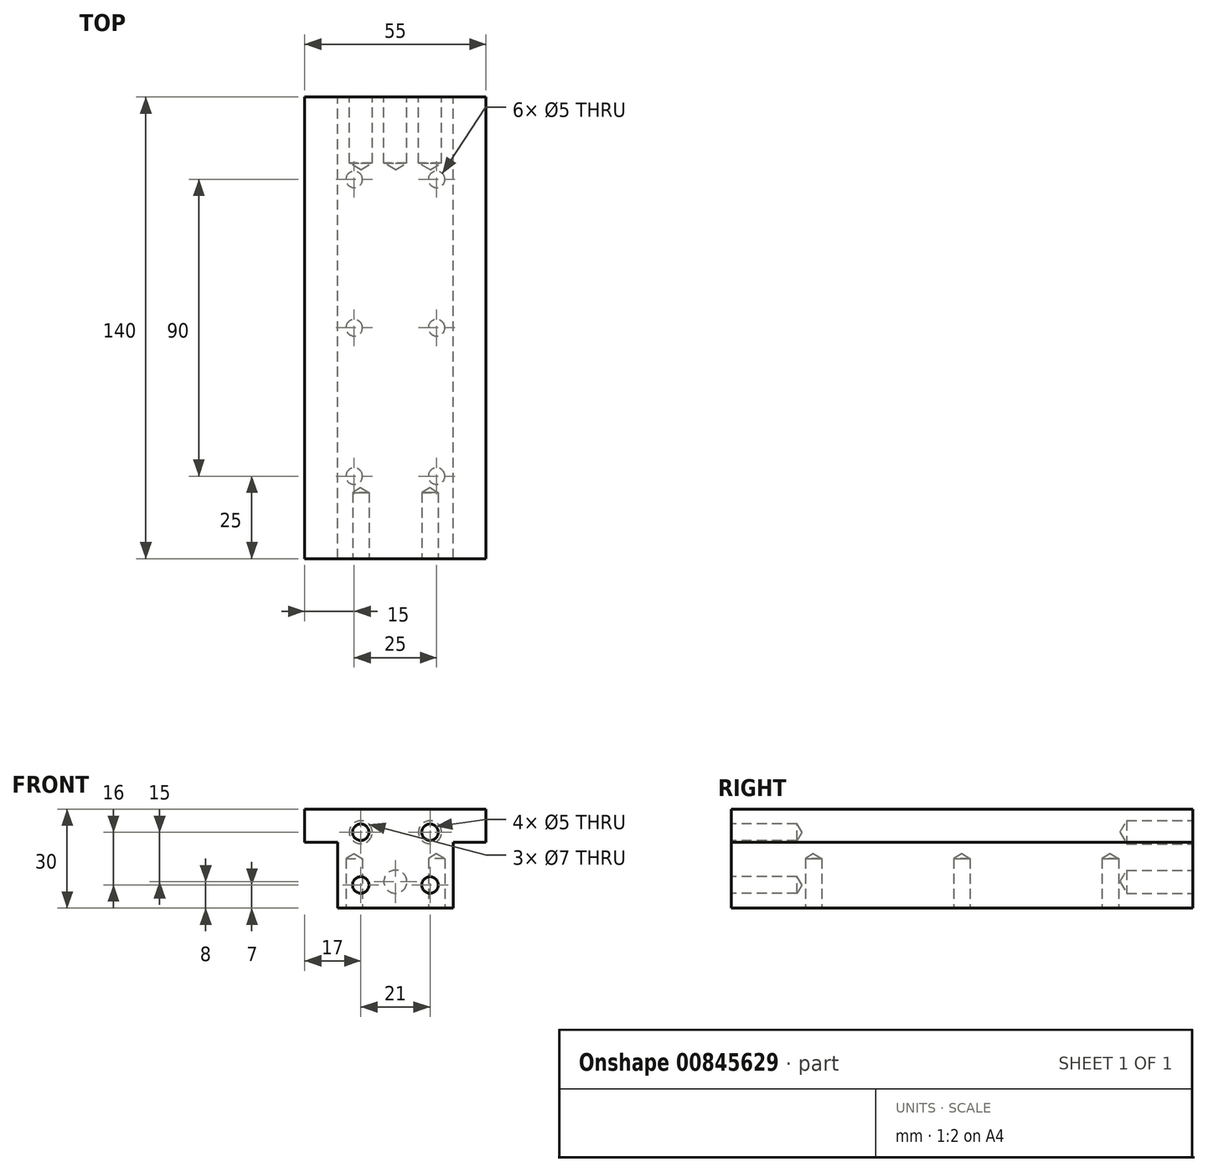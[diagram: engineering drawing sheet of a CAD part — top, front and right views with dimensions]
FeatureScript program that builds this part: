
annotation { "Feature Type Name" : "Feature", "Feature Type Description" : "" }
export const myFeature = defineFeature(function(context is Context, id is Id, definition is map)
    precondition{}
    {
        {
            var Q0;
            Q0=qCreatedBy(makeId("Front.planeOp"),FACE);
            var sketch = newSketch(context, id + "F0", { "sketchPlane" : qUnion([Q0])});
            skLineSegment(sketch, "E0", {"start": v(0, 10) * mm, "end": v(-27.5, 10) * mm});
            skLineSegment(sketch, "E1", {"start": v(-27.5, 10) * mm, "end": v(-27.5, 0) * mm});
            skLineSegment(sketch, "E2", {"start": v(-27.5, 0) * mm, "end": v(-17.5, 0) * mm});
            skLineSegment(sketch, "E3", {"start": v(-17.5, 0) * mm, "end": v(-17.5, -20) * mm});
            skLineSegment(sketch, "E4", {"start": v(-17.5, -20) * mm, "end": v(0, -20) * mm});
            skLineSegment(sketch, "E5", {"start": v(0, -20) * mm, "end": v(0, 10) * mm});
            skSolve(sketch);
        }
        {
            var Q0;
            Q0=makeQuery(id+"F0.imprint","IMPRINT",FACE,{"disambiguationData":[TD([[makeQuery(id+"F0.imprint","IMPRINT",EDGE,{"derivedFrom":sQuery(id+"F0.wireOp",EDGE,"E0")}),1.0]])]});
            extrude(context, id + "F1", {"entities" : qUnion([Q0]), "endBound" : BoundingType.SYMMETRIC, "depth" : 140 * mm, "offsetDistance" : 25 * mm});
        }
        {
            var Q0;
            Q0=makeQuery(id+"F1.opExtrude","CAP_FACE",FACE,{"disambiguationData":[OSD([sQuery(id+"F0.wireOp",EDGE,"E0"),sQuery(id+"F0.wireOp",EDGE,"E1"),sQuery(id+"F0.wireOp",EDGE,"E2"),sQuery(id+"F0.wireOp",EDGE,"E3"),sQuery(id+"F0.wireOp",EDGE,"E4"),sQuery(id+"F0.wireOp",EDGE,"E5")])],"isStart":false});
            var sketch = newSketch(context, id + "F2", { "sketchPlane" : qUnion([Q0])});
            skLineSegment(sketch, "E6", {"start": v(-10.5, 3) * mm, "end": v(-10.5, -13) * mm, "construction": true});
            skSolve(sketch);
        }
        {
            var Q0;
            Q0=sQuery(id+"F2.wireOp",VERTEX,"E6.start");
            var Q1;
            Q1=sQuery(id+"F2.wireOp",VERTEX,"E6.end");
            var Q2;
            Q2=makeQuery(id+"F1.opExtrude","SWEPT_BODY",BODY,{"disambiguationData":[OSD([sQuery(id+"F0.wireOp",EDGE,"E0"),sQuery(id+"F0.wireOp",EDGE,"E1"),sQuery(id+"F0.wireOp",EDGE,"E2"),sQuery(id+"F0.wireOp",EDGE,"E3"),sQuery(id+"F0.wireOp",EDGE,"E4"),sQuery(id+"F0.wireOp",EDGE,"E5")])]});
            hole(context, id + "F3", {"style" : HoleStyle.SIMPLE, "endStyle" : HoleEndStyle.BLIND, "standardTappedOrClearance" : lookupTablePath({ "standard" : "ISO", "engagement" : "75%", "pitch" : "1 mm", "size" : "M6", "type" : "Tapped" }), "standardBlindInLast" : lookupTablePath({ "standard" : "ISO", "engagement" : "75%", "pitch" : "1 mm", "size" : "M6", "type" : "Tapped" }), "holeDiameter" : 5 * mm, "majorDiameter" : 6 * mm, "showTappedDepth" : true, "holeDepth" : 20 * mm, "isTappedThrough" : true, "tappedDepth" : 15 * mm, "tapClearance" : 5, "startFromSketch" : true, "locations" : qUnion([Q0, Q1]), "scope" : qUnion([Q2])});
        }
        {
            var Q0;
            Q0=makeQuery(id+"F1.opExtrude","SWEPT_FACE",FACE,{"disambiguationData":[OSD([sQuery(id+"F0.wireOp",EDGE,"E4")])]});
            var sketch = newSketch(context, id + "F4", { "sketchPlane" : qUnion([Q0])});
            skLineSegment(sketch, "E7", {"start": v(-12.5, 45) * mm, "end": v(-12.5, -45) * mm, "construction": true});
            skPoint(sketch, "E8", {"position": v(-12.5, 0) * mm});
            skSolve(sketch);
        }
        {
            var Q0;
            Q0=sQuery(id+"F4.wireOp",VERTEX,"E7.start");
            var Q1;
            Q1=sQuery(id+"F4.wireOp",VERTEX,"E8");
            var Q2;
            Q2=sQuery(id+"F4.wireOp",VERTEX,"E7.end");
            var Q3;
            Q3=makeQuery(id+"F1.opExtrude","SWEPT_BODY",BODY,{"disambiguationData":[OSD([sQuery(id+"F0.wireOp",EDGE,"E0"),sQuery(id+"F0.wireOp",EDGE,"E1"),sQuery(id+"F0.wireOp",EDGE,"E2"),sQuery(id+"F0.wireOp",EDGE,"E3"),sQuery(id+"F0.wireOp",EDGE,"E4"),sQuery(id+"F0.wireOp",EDGE,"E5")])]});
            hole(context, id + "F5", {"style" : HoleStyle.SIMPLE, "endStyle" : HoleEndStyle.BLIND, "standardTappedOrClearance" : lookupTablePath({ "standard" : "ISO", "engagement" : "75%", "pitch" : "1 mm", "size" : "M6", "type" : "Tapped" }), "standardBlindInLast" : lookupTablePath({ "standard" : "ISO", "engagement" : "75%", "pitch" : "1 mm", "size" : "M6", "type" : "Tapped" }), "holeDiameter" : 5 * mm, "majorDiameter" : 6 * mm, "showTappedDepth" : true, "holeDepth" : 15 * mm, "isTappedThrough" : true, "tappedDepth" : 10 * mm, "tapClearance" : 5, "startFromSketch" : true, "locations" : qUnion([Q0, Q1, Q2]), "scope" : qUnion([Q3])});
        }
        {
            var Q0;
            Q0=makeQuery(id+"F1.opExtrude","SWEPT_BODY",BODY,{"disambiguationData":[OSD([sQuery(id+"F0.wireOp",EDGE,"E0"),sQuery(id+"F0.wireOp",EDGE,"E1"),sQuery(id+"F0.wireOp",EDGE,"E2"),sQuery(id+"F0.wireOp",EDGE,"E3"),sQuery(id+"F0.wireOp",EDGE,"E4"),sQuery(id+"F0.wireOp",EDGE,"E5")])]});
            var Q1;
            Q1=qCreatedBy(makeId("Right.planeOp"),FACE);
            mirror(context, id + "F6", {"operationType" : NewBodyOperationType.ADD, "entities" : qUnion([Q0]), "mirrorPlane" : qUnion([Q1])});
        }
        {
            var Q0;
            {var subQ0=makeQuery(id+"F1.opExtrude","CAP_FACE",FACE,{"disambiguationData":[OSD([sQuery(id+"F0.wireOp",EDGE,"E0"),sQuery(id+"F0.wireOp",EDGE,"E1"),sQuery(id+"F0.wireOp",EDGE,"E2"),sQuery(id+"F0.wireOp",EDGE,"E3"),sQuery(id+"F0.wireOp",EDGE,"E4"),sQuery(id+"F0.wireOp",EDGE,"E5")])],"isStart":true});Q0=makeQuery(id+"F6.boolean.opBoolean","MERGE",FACE,{"derivedFrom":[subQ0,makeQuery(id+"F6.opPattern","COPY",FACE,{"derivedFrom":subQ0,"instanceName":"1"})]});}
            var sketch = newSketch(context, id + "F7", { "sketchPlane" : qUnion([Q0])});
            skLineSegment(sketch, "E9", {"start": v(-10.5, 3) * mm, "end": v(10.5, 3) * mm, "construction": true});
            skPoint(sketch, "E10", {"position": v(0, -12) * mm});
            skSolve(sketch);
        }
        {
            var Q0;
            Q0=sQuery(id+"F7.wireOp",VERTEX,"E9.start");
            var Q1;
            Q1=sQuery(id+"F7.wireOp",VERTEX,"E9.end");
            var Q2;
            Q2=sQuery(id+"F7.wireOp",VERTEX,"E10");
            var Q3;
            Q3=makeQuery(id+"F1.opExtrude","SWEPT_BODY",BODY,{"disambiguationData":[OSD([sQuery(id+"F0.wireOp",EDGE,"E0"),sQuery(id+"F0.wireOp",EDGE,"E1"),sQuery(id+"F0.wireOp",EDGE,"E2"),sQuery(id+"F0.wireOp",EDGE,"E3"),sQuery(id+"F0.wireOp",EDGE,"E4"),sQuery(id+"F0.wireOp",EDGE,"E5")])]});
            hole(context, id + "F8", {"style" : HoleStyle.SIMPLE, "endStyle" : HoleEndStyle.BLIND, "standardTappedOrClearance" : lookupTablePath({ "standard" : "ISO", "engagement" : "75%", "pitch" : "1 mm", "size" : "M8", "type" : "Tapped" }), "standardBlindInLast" : lookupTablePath({ "standard" : "ISO", "engagement" : "75%", "pitch" : "1 mm", "size" : "M8", "type" : "Tapped" }), "holeDiameter" : 7 * mm, "majorDiameter" : 8 * mm, "showTappedDepth" : true, "holeDepth" : 20 * mm, "isTappedThrough" : true, "tappedDepth" : 15 * mm, "tapClearance" : 5, "startFromSketch" : true, "locations" : qUnion([Q0, Q1, Q2]), "scope" : qUnion([Q3])});
        }
    });
